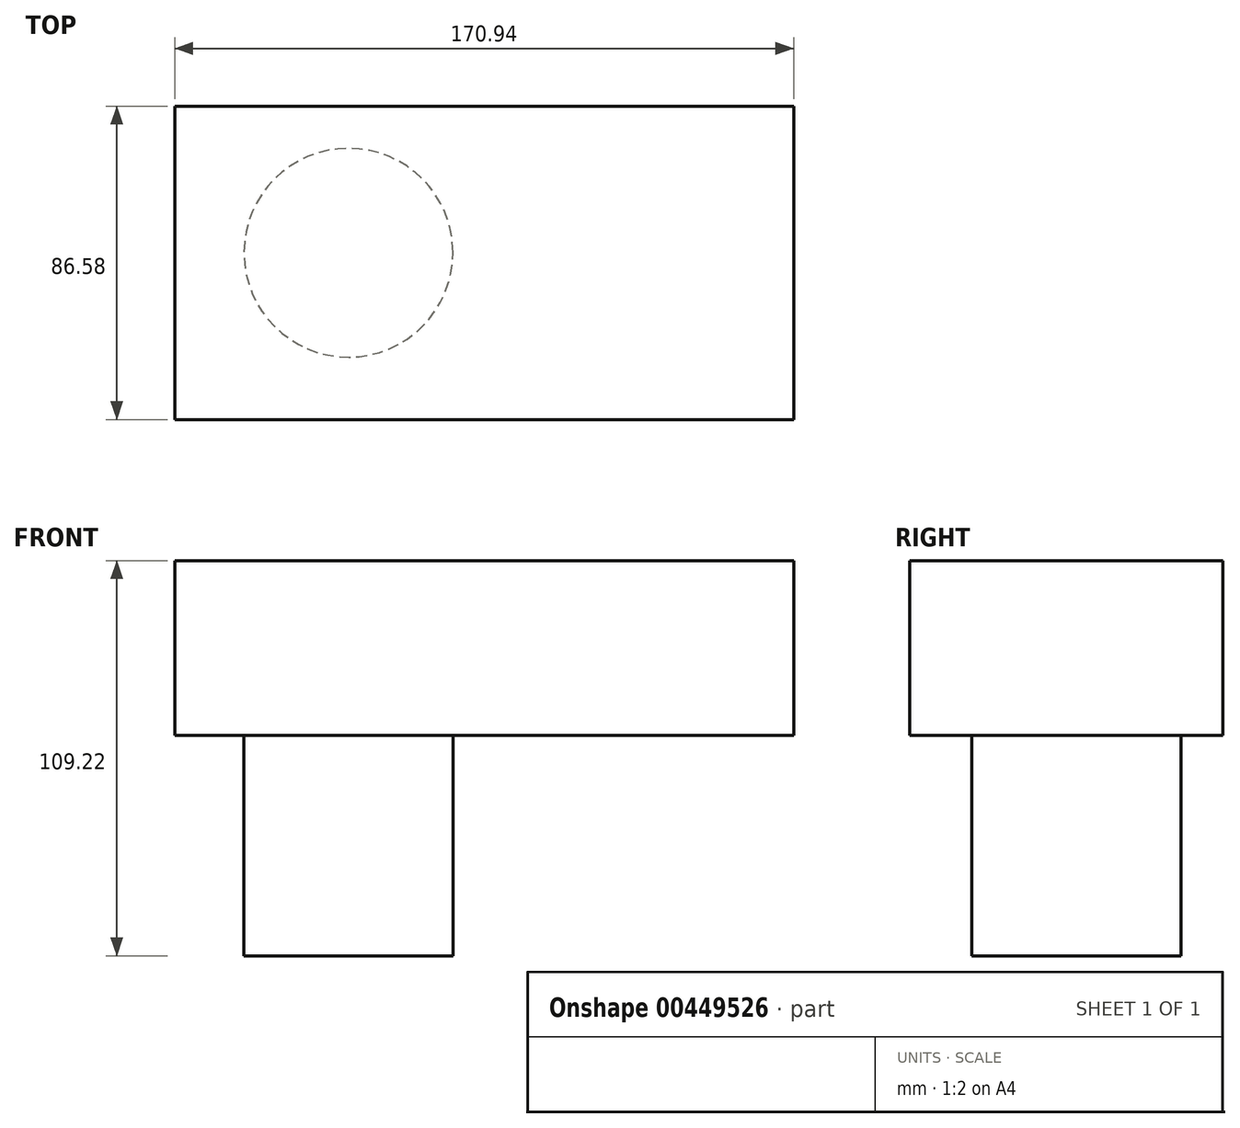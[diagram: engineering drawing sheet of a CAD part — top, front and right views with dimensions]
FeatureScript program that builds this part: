
annotation { "Feature Type Name" : "Feature", "Feature Type Description" : "" }
export const myFeature = defineFeature(function(context is Context, id is Id, definition is map)
    precondition{}
    {
        {
            var Q0;
            Q0=qCreatedBy(makeId("Top.planeOp"),FACE);
            var sketch = newSketch(context, id + "F0", { "sketchPlane" : qUnion([Q0])});
            skLineSegment(sketch, "E0.bottom", {"start": v(-134.38, 24.6) * mm, "end": v(36.56, 24.6) * mm});
            skLineSegment(sketch, "E0.top", {"start": v(-134.38, -61.99) * mm, "end": v(36.56, -61.99) * mm});
            skLineSegment(sketch, "E0.left", {"start": v(-134.38, 24.6) * mm, "end": v(-134.38, -61.99) * mm});
            skLineSegment(sketch, "E0.right", {"start": v(36.56, 24.6) * mm, "end": v(36.56, -61.99) * mm});
            skSolve(sketch);
        }
        {
            var Q0;
            Q0 = qSketchRegion(id + "F0", true);
            var Q1;
            Q1=makeQuery(id+"F0.imprint","IMPRINT",FACE,{"disambiguationData":[TD([[makeQuery(id+"F0.imprint","IMPRINT",EDGE,{"derivedFrom":sQuery(id+"F0.wireOp",EDGE,"E0.bottom")}),-1.0]])]});
            extrude(context, id + "F1", {"entities" : qUnion([Q0, Q1]), "depth" : 48.26 * mm});
        }
        {
            var Q0;
            Q0=makeQuery(id+"F1.opExtrude","CAP_FACE",FACE,{"disambiguationData":[OSD([sQuery(id+"F0.wireOp",EDGE,"E0.bottom"),sQuery(id+"F0.wireOp",EDGE,"E0.top"),sQuery(id+"F0.wireOp",EDGE,"E0.left"),sQuery(id+"F0.wireOp",EDGE,"E0.right")])],"isStart":false});
            var sketch = newSketch(context, id + "F2", { "sketchPlane" : qUnion([Q0])});
            skCircle(sketch, "E1", {"center": v(-86.38, -15.9) * mm, "radius": 28.85 * mm});
            skSolve(sketch);
        }
        {
            var Q0;
            Q0 = qSketchRegion(id + "F2", true);
            extrude(context, id + "F3", {"entities" : qUnion([Q0]), "operationType" : NewBodyOperationType.ADD, "oppositeDirection" : true, "depth" : 109.22 * mm});
        }
    });
